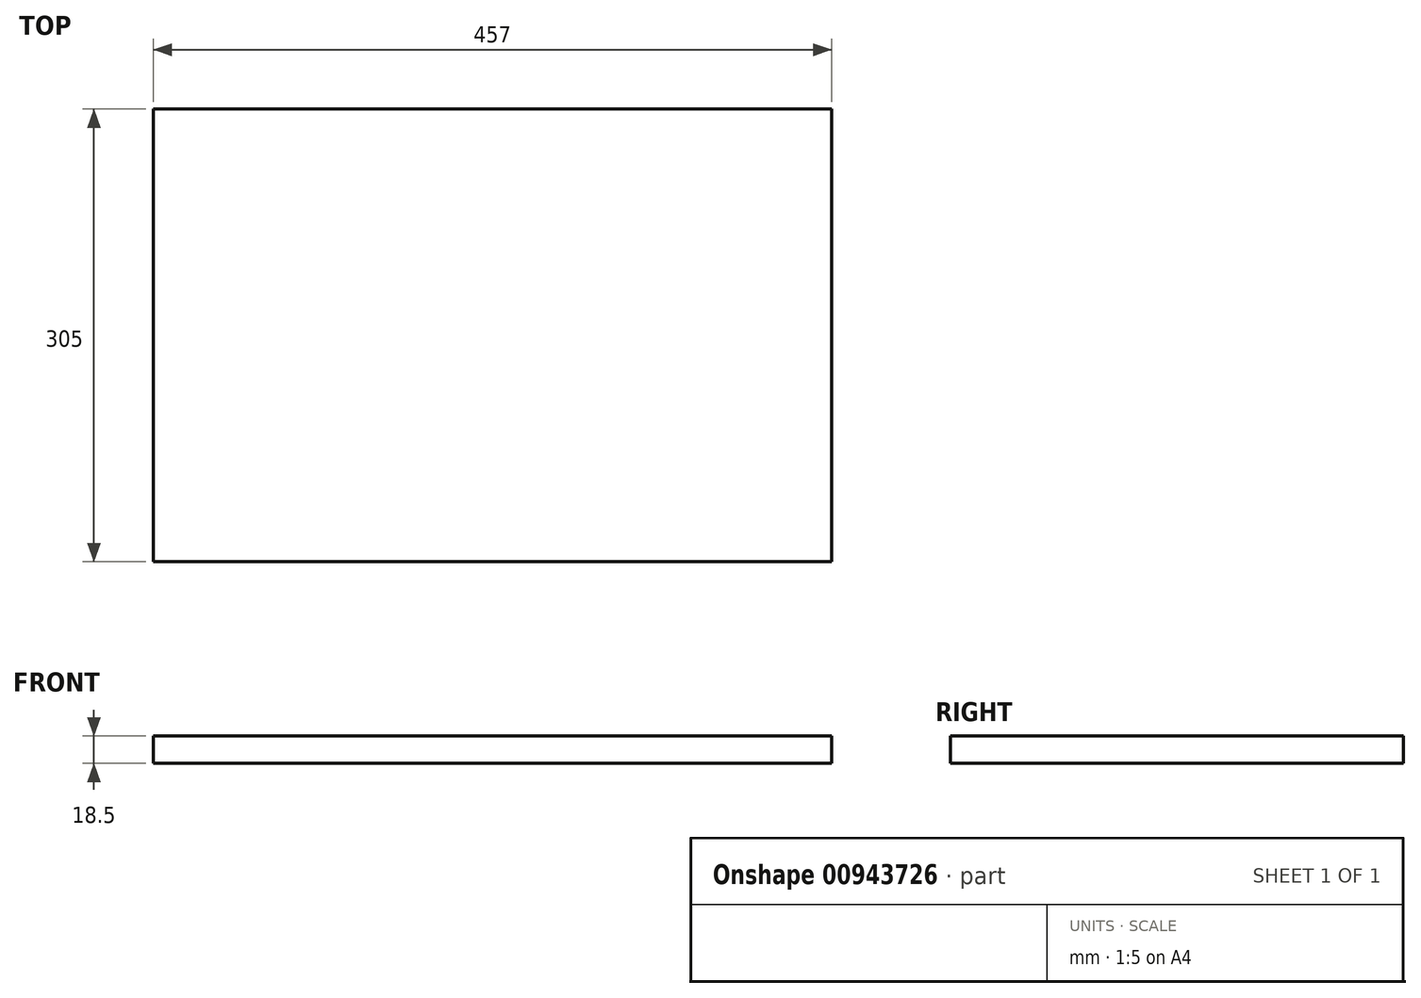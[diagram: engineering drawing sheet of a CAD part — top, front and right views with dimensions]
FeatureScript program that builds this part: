
annotation { "Feature Type Name" : "Feature", "Feature Type Description" : "" }
export const myFeature = defineFeature(function(context is Context, id is Id, definition is map)
    precondition{}
    {
        {
            var Q0;
            Q0=qCreatedBy(makeId("Top.planeOp"),FACE);
            var sketch = newSketch(context, id + "F0", { "sketchPlane" : qUnion([Q0])});
            skLineSegment(sketch, "E0.bottom", {"start": v(0, 0) * mm, "end": v(457, 0) * mm});
            skLineSegment(sketch, "E0.top", {"start": v(0, 305) * mm, "end": v(457, 305) * mm});
            skLineSegment(sketch, "E0.left", {"start": v(0, 0) * mm, "end": v(0, 305) * mm});
            skLineSegment(sketch, "E0.right", {"start": v(457, 0) * mm, "end": v(457, 305) * mm});
            skSolve(sketch);
        }
        {
            var Q0;
            Q0=makeQuery(id+"F0.imprint","IMPRINT",FACE,{"disambiguationData":[TD([[makeQuery(id+"F0.imprint","IMPRINT",EDGE,{"derivedFrom":sQuery(id+"F0.wireOp",EDGE,"E0.bottom")}),1.0]])]});
            extrude(context, id + "F1", {"entities" : qUnion([Q0]), "depth" : 18.5 * mm, "offsetDistance" : 25 * mm});
        }
    });
